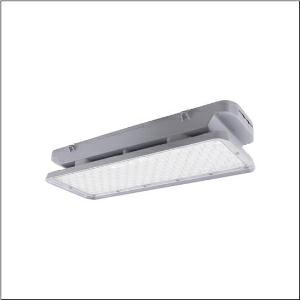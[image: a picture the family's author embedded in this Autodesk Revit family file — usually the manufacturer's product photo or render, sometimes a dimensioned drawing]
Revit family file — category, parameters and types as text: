
# Revit family: highbay_21-s_51hk42da4jca
name_source: partatom
category: Lighting Fixtures
units: mm (PartAtom-declared; Revit-internal decimal feet)

## family parameters
Cut with Voids When Loaded = No
Host = Face
Light Source = No
Part Type = Normal
Room Calculation Point = No
Round Connector Dimension = Use Diameter
Shared = No

## types (1)
- Highbay 21-S (1 x LED, 19200 lm, 107 W, 4000K)
    Apparent Load = 107 VA
    CIE Flux Codes = 74 96 100 100 100
    Color Rendering = 80
    Color Temperature = 4000K
    Default Elevation = 1800 mm
    Description = Highbay 21-S, LED high bay luminaire, primary light control with lens, of PC, primary optical cover: cover panel, light emission: direct distribution, primary light characteristic: symmetric, installation type: suspended mounting, surface-mounted, LED, rated luminous flux: 19.200lm, luminous efficacy: 160lm/W, light colour: 840, colour temperature: 4000K, control gear: ECG DALI, with terminal, 5-pole, max. 2.5mm², mains connection: 220..240V, AC, 50Hz, rated input power: 120W, housing, of diecast aluminium, coated, grey, length: 471mm, width: 172mm, height: 87mm, protection rating (complete): IP66, insulation class (complete): insulation class I (protective earthing), certification: CE, ENEC, UKCA, protection symbol: D, impact resistance: IK08, permissible operating ambient temperature: -30..+55°C, corresponds to IFS (International Featured Standards) requirements for safety and quality in the food industry, LABS conformity tested according to VDMA 24364:2018-05, packaging unit: 1 piece
    Height = 89 mm
    Lamp = 1 x LED
    Lamp Light Flux = 19200 lm
    Lamp Power = 107 W
    Lamp count = 1
    Length = 471 mm
    Luminous efficacy = 179 lm/W
    Manufacturer = Siteco
    ModVariant = No
    Model = 51HK42DA4JCA
    Mounting Place = Ceiling
    Mounting Type = Pendant
    Number of Poles = 1
    OnlyDefault = Yes
    Power Factor = 1
    Product Name = Highbay 21-S
    Product group = LED high bay luminaire
    ProductGroupID = 903
    Protection Class = Protection class I
    Protection Degree = IP 66
    RLX_Detail_Level = 1
    RLX_Emergency_Light_Flux = 0 lm
    RLX_Emergency_Type = 0
    RLX_Emergency_Type_DB = No
    RlxData = <blob elided: 22057 chars, md5=770ce51a>
    Socket = socket
    Standby Power = 0 W
    System Light Flux = 19200 lm
    System Power = 107 W
    Type Comments = Product without accessories
    Type Image = l_1276526.jpg
    URL = http://relux.com
    VarID = ---
    Voltage = 0 V
    Weight = 0.00 kg
    Width = 172 mm

## geometry (parser evidence)
native form markers: Blend x4, Sweep x10
no freeform markers — native parametric forms only
